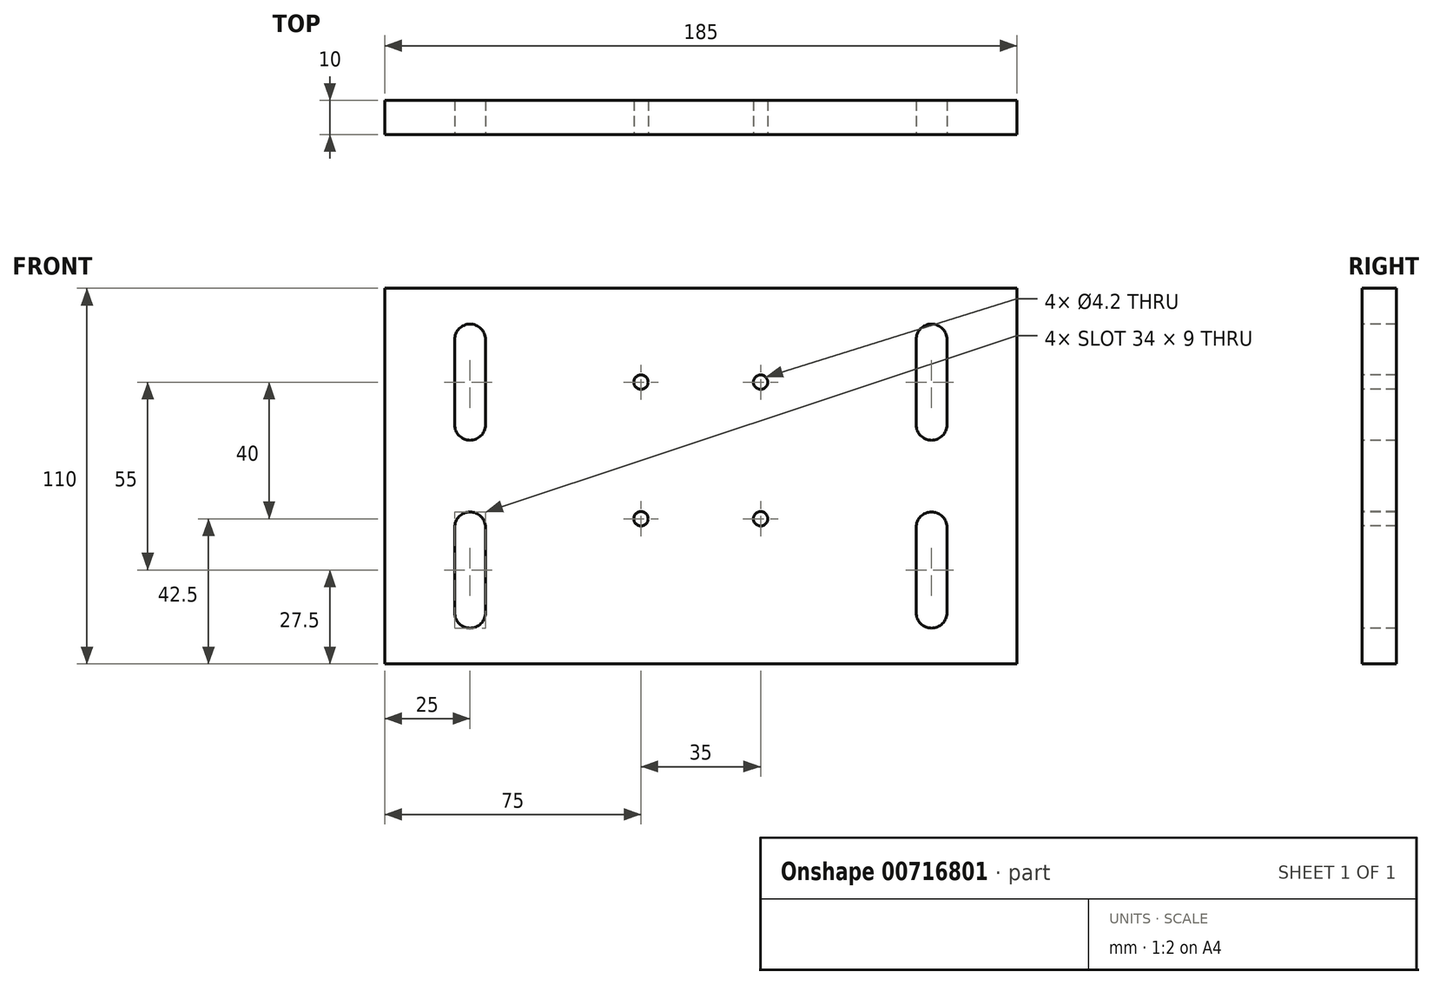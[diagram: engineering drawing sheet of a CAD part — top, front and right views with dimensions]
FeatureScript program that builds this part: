
annotation { "Feature Type Name" : "Feature", "Feature Type Description" : "" }
export const myFeature = defineFeature(function(context is Context, id is Id, definition is map)
    precondition{}
    {
        {
            var Q0;
            Q0=qCreatedBy(makeId("Front.planeOp"),FACE);
            var sketch = newSketch(context, id + "F0", { "sketchPlane" : qUnion([Q0])});
            skLineSegment(sketch, "E0.bottom", {"start": v(-92.5, 55) * mm, "end": v(92.5, 55) * mm});
            skLineSegment(sketch, "E0.top", {"start": v(-92.5, -55) * mm, "end": v(92.5, -55) * mm});
            skLineSegment(sketch, "E0.left", {"start": v(-92.5, 55) * mm, "end": v(-92.5, -55) * mm});
            skLineSegment(sketch, "E0.right", {"start": v(92.5, 55) * mm, "end": v(92.5, -55) * mm});
            skPoint(sketch, "E0.middle", {"position": v(0, 0) * mm});
            skSolve(sketch);
        }
        {
            var Q0;
            Q0 = qSketchRegion(id + "F0", true);
            extrude(context, id + "F1", {"entities" : qUnion([Q0]), "endBound" : BoundingType.SYMMETRIC, "depth" : 10 * mm, "offsetDistance" : 25 * mm});
        }
        {
            var Q0;
            Q0=makeQuery(id+"F1.opExtrude","CAP_FACE",FACE,{"disambiguationData":[OSD([sQuery(id+"F0.wireOp",EDGE,"E0.bottom"),sQuery(id+"F0.wireOp",EDGE,"E0.top"),sQuery(id+"F0.wireOp",EDGE,"E0.left"),sQuery(id+"F0.wireOp",EDGE,"E0.right")])],"isStart":false});
            var sketch = newSketch(context, id + "F2", { "sketchPlane" : qUnion([Q0])});
            skLineSegment(sketch, "E1", {"start": v(-67.5, 40) * mm, "end": v(-67.5, 15) * mm});
            skLineSegment(sketch, "E2", {"start": v(67.5, 40) * mm, "end": v(67.5, 15) * mm});
            skLineSegment(sketch, "E3", {"start": v(-67.5, -15) * mm, "end": v(-67.5, -40) * mm});
            skLineSegment(sketch, "E4", {"start": v(67.5, -15) * mm, "end": v(67.5, -40) * mm});
            skArc(sketch, "E5.0.startCap", {"start": v(-72, 40) * mm, "mid": v(-67.5, 44.5) * mm, "end": v(-63, 40) * mm});
            skArc(sketch, "E5.0.endCap", {"start": v(-63, 15) * mm, "mid": v(-67.5, 10.5) * mm, "end": v(-72, 15) * mm});
            skLineSegment(sketch, "E5.0.left", {"start": v(-63, 40) * mm, "end": v(-63, 15) * mm});
            skLineSegment(sketch, "E5.0.right", {"start": v(-72, 40) * mm, "end": v(-72, 15) * mm});
            skArc(sketch, "E5.1.startCap", {"start": v(-72, -15) * mm, "mid": v(-67.5, -10.5) * mm, "end": v(-63, -15) * mm});
            skArc(sketch, "E5.1.endCap", {"start": v(-63, -40) * mm, "mid": v(-67.5, -44.5) * mm, "end": v(-72, -40) * mm});
            skLineSegment(sketch, "E5.1.left", {"start": v(-63, -15) * mm, "end": v(-63, -40) * mm});
            skLineSegment(sketch, "E5.1.right", {"start": v(-72, -15) * mm, "end": v(-72, -40) * mm});
            skArc(sketch, "E5.2.startCap", {"start": v(63, 40) * mm, "mid": v(67.5, 44.5) * mm, "end": v(72, 40) * mm});
            skArc(sketch, "E5.2.endCap", {"start": v(72, 15) * mm, "mid": v(67.5, 10.5) * mm, "end": v(63, 15) * mm});
            skLineSegment(sketch, "E5.2.left", {"start": v(72, 40) * mm, "end": v(72, 15) * mm});
            skLineSegment(sketch, "E5.2.right", {"start": v(63, 40) * mm, "end": v(63, 15) * mm});
            skArc(sketch, "E5.3.startCap", {"start": v(63, -15) * mm, "mid": v(67.5, -10.5) * mm, "end": v(72, -15) * mm});
            skArc(sketch, "E5.3.endCap", {"start": v(72, -40) * mm, "mid": v(67.5, -44.5) * mm, "end": v(63, -40) * mm});
            skLineSegment(sketch, "E5.3.left", {"start": v(72, -15) * mm, "end": v(72, -40) * mm});
            skLineSegment(sketch, "E5.3.right", {"start": v(63, -15) * mm, "end": v(63, -40) * mm});
            skSolve(sketch);
        }
        {
            var Q0;
            Q0 = qSketchRegion(id + "F2", true);
            extrude(context, id + "F3", {"entities" : qUnion([Q0]), "operationType" : NewBodyOperationType.REMOVE, "endBound" : BoundingType.THROUGH_ALL, "oppositeDirection" : true, "depth" : 25 * mm, "offsetDistance" : 25 * mm});
        }
        {
            var Q0;
            Q0=makeQuery(id+"F1.opExtrude","CAP_FACE",FACE,{"disambiguationData":[OSD([sQuery(id+"F0.wireOp",EDGE,"E0.bottom"),sQuery(id+"F0.wireOp",EDGE,"E0.top"),sQuery(id+"F0.wireOp",EDGE,"E0.left"),sQuery(id+"F0.wireOp",EDGE,"E0.right")])],"isStart":false});
            var sketch = newSketch(context, id + "F4", { "sketchPlane" : qUnion([Q0])});
            skPoint(sketch, "E6", {"position": v(-17.5, 27.5) * mm});
            skPoint(sketch, "E7", {"position": v(17.5, 27.5) * mm});
            skPoint(sketch, "E8", {"position": v(17.5, -12.5) * mm});
            skPoint(sketch, "E9", {"position": v(-17.5, -12.5) * mm});
            skSolve(sketch);
        }
        {
            var Q0;
            Q0=sQuery(id+"F4.wireOp",VERTEX,"E6");
            var Q1;
            Q1=sQuery(id+"F4.wireOp",VERTEX,"E9");
            var Q2;
            Q2=sQuery(id+"F4.wireOp",VERTEX,"E7");
            var Q3;
            Q3=sQuery(id+"F4.wireOp",VERTEX,"E8");
            var Q4;
            Q4=makeQuery(id+"F1.opExtrude","SWEPT_BODY",BODY,{"disambiguationData":[OSD([sQuery(id+"F0.wireOp",EDGE,"E0.bottom"),sQuery(id+"F0.wireOp",EDGE,"E0.top"),sQuery(id+"F0.wireOp",EDGE,"E0.left"),sQuery(id+"F0.wireOp",EDGE,"E0.right")])]});
            hole(context, id + "F5", {"style" : HoleStyle.SIMPLE, "endStyle" : HoleEndStyle.BLIND, "standardTappedOrClearance" : lookupTablePath({ "standard" : "ISO", "engagement" : "75%", "pitch" : "0.8 mm", "size" : "M5", "type" : "Tapped" }), "standardBlindInLast" : lookupTablePath({ "standard" : "ISO", "engagement" : "75%", "pitch" : "0.8 mm", "size" : "M5", "type" : "Tapped" }), "holeDiameter" : 4.2 * mm, "majorDiameter" : 5 * mm, "showTappedDepth" : true, "holeDepth" : 17.4 * mm, "isTappedThrough" : true, "tappedDepth" : 15 * mm, "tapClearance" : 3, "startFromSketch" : true, "locations" : qUnion([Q0, Q1, Q2, Q3]), "scope" : qUnion([Q4])});
        }
    });
